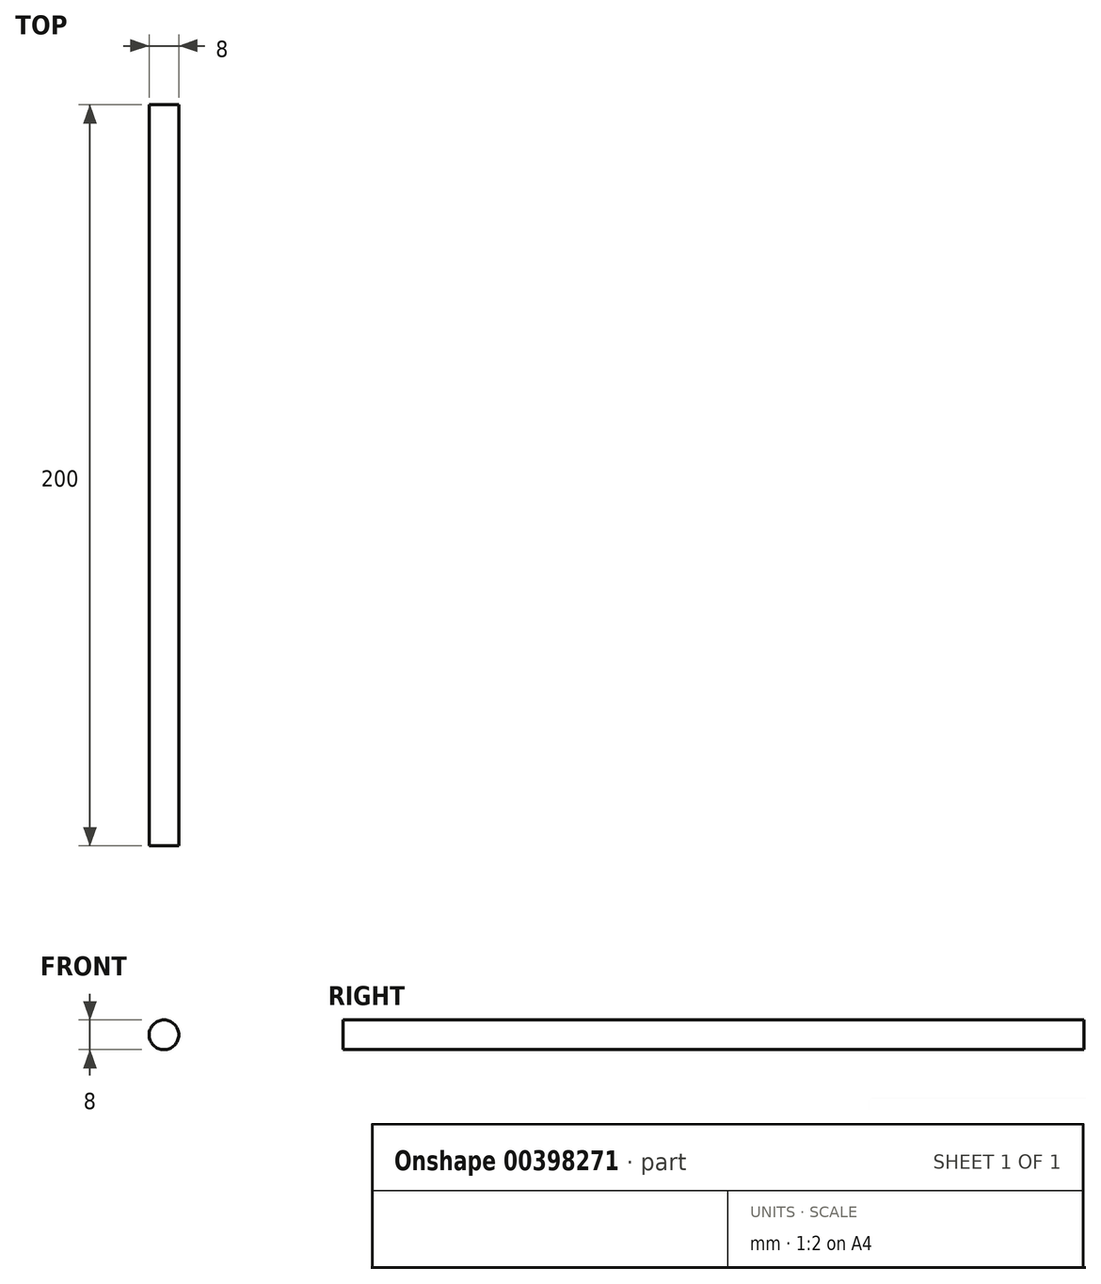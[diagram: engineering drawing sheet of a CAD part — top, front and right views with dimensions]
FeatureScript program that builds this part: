
annotation { "Feature Type Name" : "Feature", "Feature Type Description" : "" }
export const myFeature = defineFeature(function(context is Context, id is Id, definition is map)
    precondition{}
    {
        {
            var Q0;
            Q0=qCreatedBy(makeId("Front.planeOp"),FACE);
            var sketch = newSketch(context, id + "F0", { "sketchPlane" : qUnion([Q0])});
            skCircle(sketch, "E0", {"center": v(0, 0) * mm, "radius": 4 * mm});
            skSolve(sketch);
        }
        {
            var Q0;
            Q0 = qSketchRegion(id + "F0", true);
            extrude(context, id + "F1", {"entities" : qUnion([Q0]), "oppositeDirection" : true, "depth" : 200 * mm});
        }
    });
